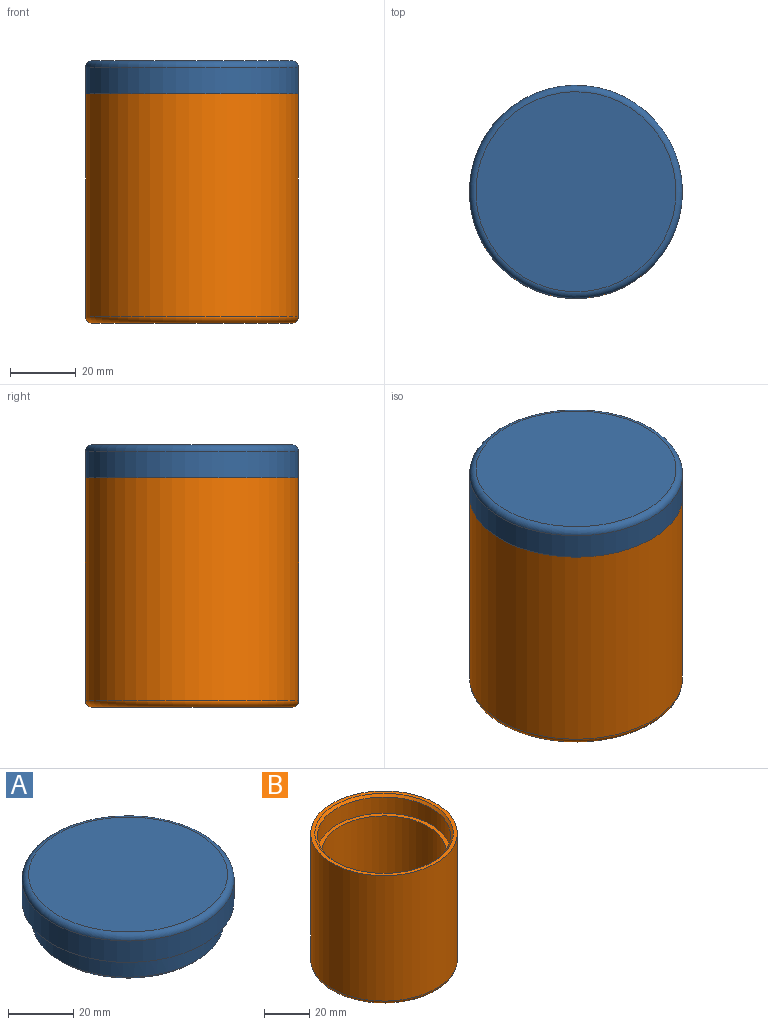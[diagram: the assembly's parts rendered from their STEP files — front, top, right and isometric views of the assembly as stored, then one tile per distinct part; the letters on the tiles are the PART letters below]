
ASSEMBLY  parts=2 mates=1
PART A: 7 faces, bbox 70.4x70.4x19 mm
  f0: cylinder r=32.5mm len=65mm, axis (0,0,1), area 1633.6mm2, adj f2,f3
  f1: plane 61x61mm, normal (0,0,1), area 2922.5mm2, adj f3
  f2: plane 65x65mm, normal (0,0,-1), area 621.3mm2, adj f0,f4
  f3: torus R=30.5mm, axis (0,0,1), area 627.2mm2, adj f0,f1
  f4: cylinder r=29.3mm len=58.6mm, axis (0,0,-1), area 1436mm2, adj f2,f6
  f5: plane 56.2x56.2mm, normal (0,0,-1), area 2480.6mm2, adj f6
  f6: cone r=28.1mm half-angle=45deg, axis (0,0,1), area 306mm2, adj f4,f5
PART B: 9 faces, bbox 70.4x70.4x70 mm
  f0: cylinder r=32.5mm len=68mm, axis (0,0,-1), area 13885.8mm2, adj f1,f7
  f1: plane 65x65mm, normal (0,0,1), area 357.4mm2, adj f0,f8
  f2: plane 61x61mm, normal (0,0,-1), area 2922.5mm2, adj f7
  f3: cylinder r=29.5mm len=59mm, axis (0,0,1), area 1631.1mm2, adj f4,f8
  f4: plane 59x59mm, normal (0,0,1), area 358.1mm2, adj f3,f6
  f5: plane 55x55mm, normal (0,0,1), area 2375.8mm2, adj f6
  f6: cylinder r=27.5mm len=55mm, axis (0,0,-1), area 9503.3mm2, adj f4,f5
  f7: torus R=30.5mm, axis (0,0,1), area 627.2mm2, adj f0,f2
  f8: cone r=29.5mm half-angle=45deg, axis (0,0,1), area 321mm2, adj f1,f3
PLACE A t=(0,0,80)mm
PLACE B at identity fixed
MATE fastened A.f0 <-> B.f6  axis (0,0,-1) through (0,0,70)mm
